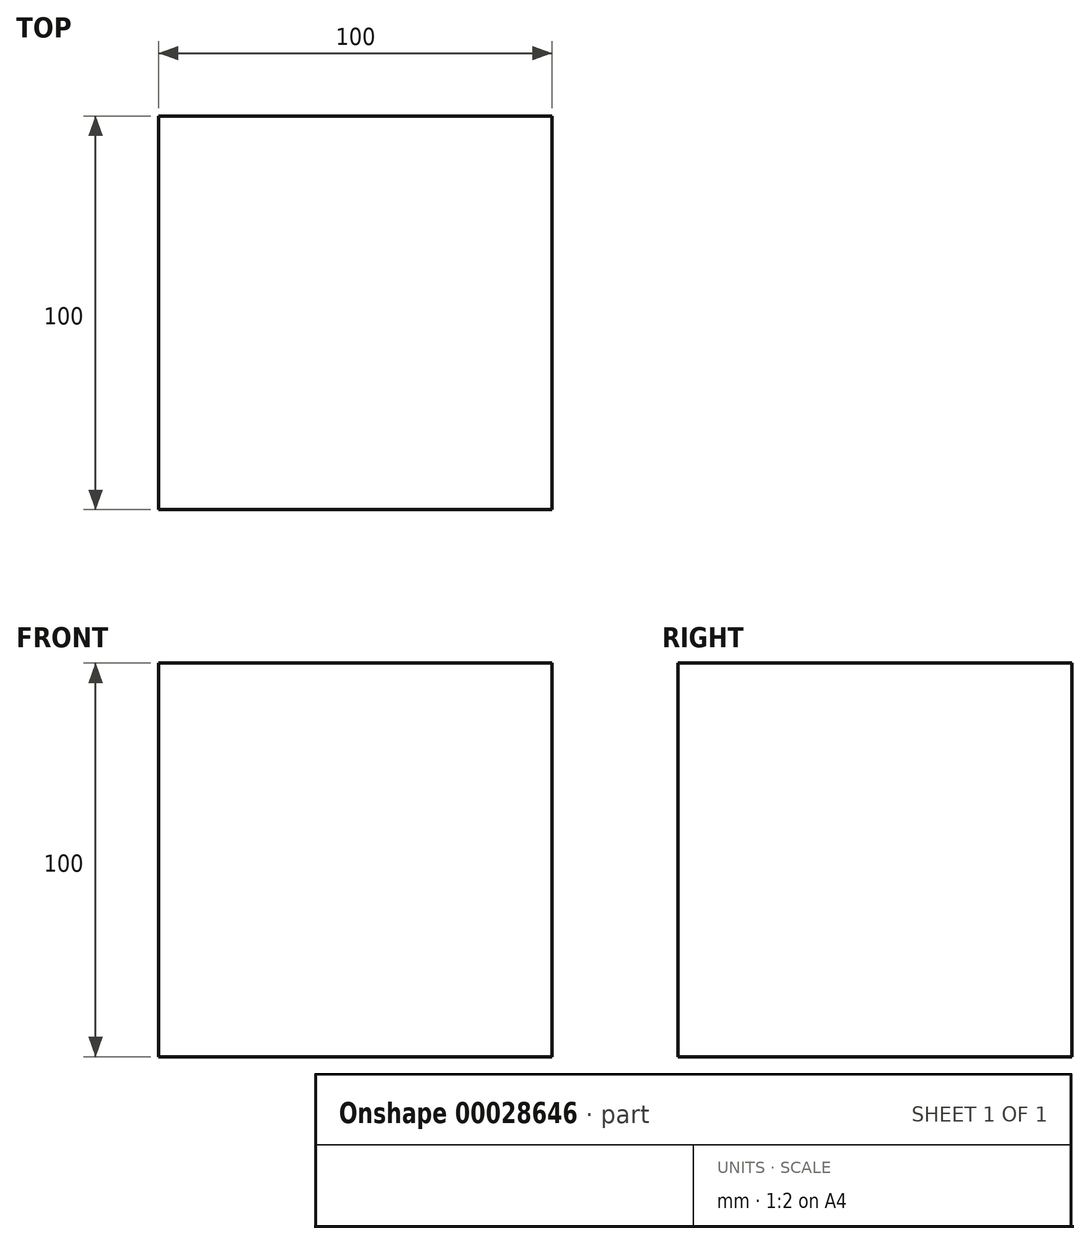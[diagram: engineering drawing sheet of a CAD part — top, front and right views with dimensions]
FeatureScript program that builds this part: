
annotation { "Feature Type Name" : "Feature", "Feature Type Description" : "" }
export const myFeature = defineFeature(function(context is Context, id is Id, definition is map)
    precondition{}
    {
        {
            var Q0;
            Q0=qCreatedBy(makeId("Front.planeOp"),FACE);
            var sketch = newSketch(context, id + "F0", { "sketchPlane" : qUnion([Q0])});
            skLineSegment(sketch, "E0.rect.bottom", {"start": v(50, 50) * mm, "end": v(-50, 50) * mm});
            skLineSegment(sketch, "E0.rect.top", {"start": v(50, -50) * mm, "end": v(-50, -50) * mm});
            skLineSegment(sketch, "E0.rect.left", {"start": v(50, 50) * mm, "end": v(50, -50) * mm});
            skLineSegment(sketch, "E0.rect.right", {"start": v(-50, 50) * mm, "end": v(-50, -50) * mm});
            skPoint(sketch, "E0.rect.middle", {"position": v(0, 0) * mm});
            skSolve(sketch);
        }
        {
            var Q0;
            Q0=makeQuery(id+"F0.imprint","IMPRINT",FACE,{"disambiguationData":[TD([[makeQuery(id+"F0.imprint","IMPRINT",EDGE,{"derivedFrom":sQuery(id+"F0.wireOp",EDGE,"E0.rect.bottom")}),1.0]])]});
            extrude(context, id + "F1", {"entities" : qUnion([Q0]), "depth" : 100 * mm});
        }
    });
